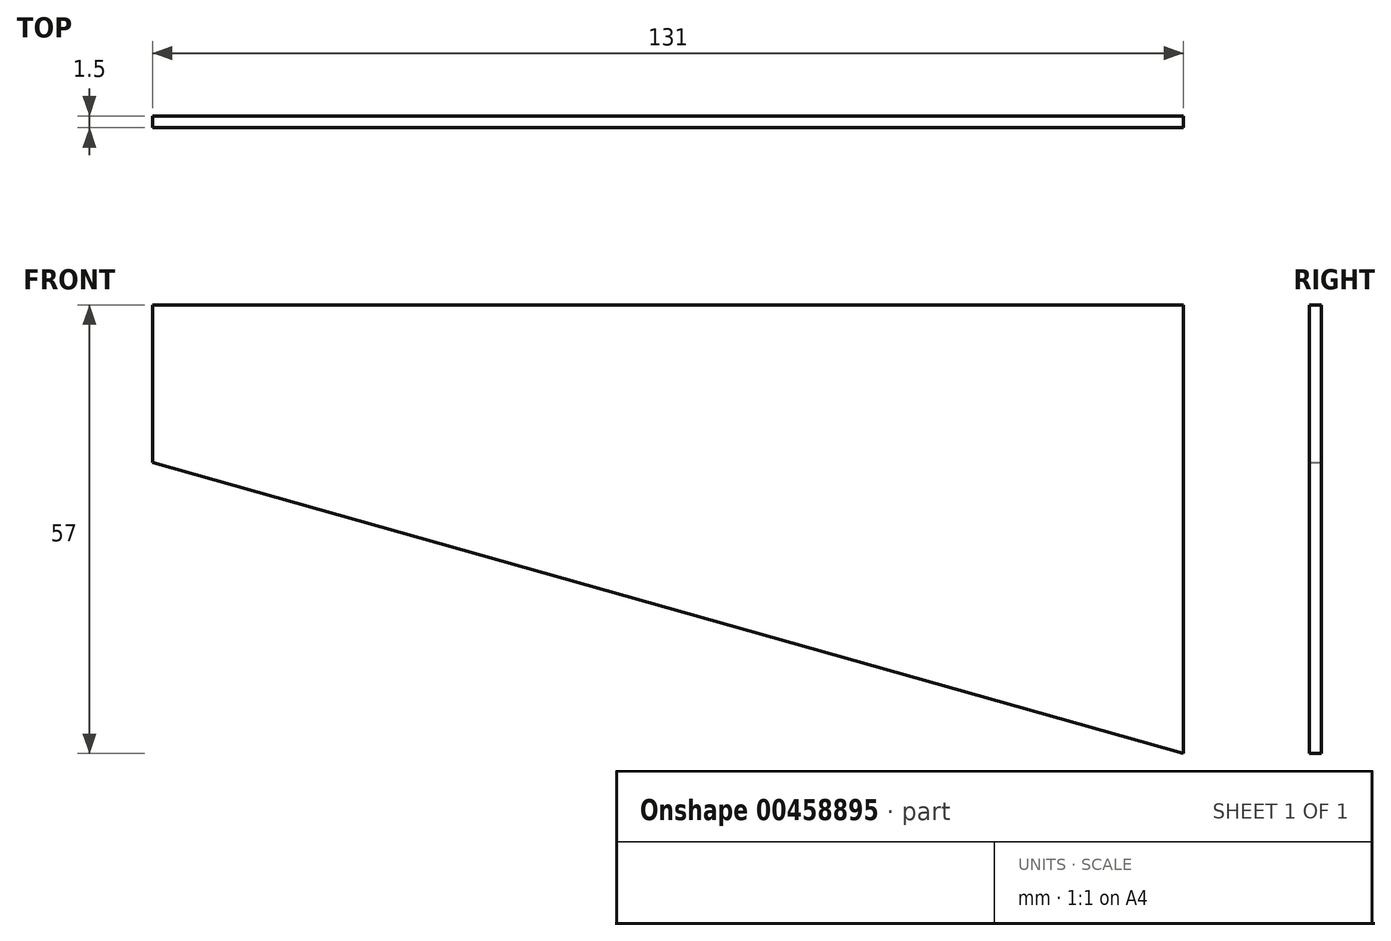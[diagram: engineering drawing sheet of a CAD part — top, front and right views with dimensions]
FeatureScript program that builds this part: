
annotation { "Feature Type Name" : "Feature", "Feature Type Description" : "" }
export const myFeature = defineFeature(function(context is Context, id is Id, definition is map)
    precondition{}
    {
        {
            var Q0;
            Q0=qCreatedBy(makeId("Front.planeOp"),FACE);
            var sketch = newSketch(context, id + "F0", { "sketchPlane" : qUnion([Q0])});
            skLineSegment(sketch, "E0", {"start": v(0, 0) * mm, "end": v(0, 20) * mm});
            skLineSegment(sketch, "E1", {"start": v(0, 20) * mm, "end": v(131, 20) * mm});
            skLineSegment(sketch, "E2", {"start": v(131, 20) * mm, "end": v(131, -37) * mm});
            skLineSegment(sketch, "E3", {"start": v(131, -37) * mm, "end": v(0, 0) * mm});
            skSolve(sketch);
        }
        {
            var Q0;
            Q0 = qSketchRegion(id + "F0", true);
            extrude(context, id + "F1", {"entities" : qUnion([Q0]), "depth" : 1.5 * mm});
        }
    });
